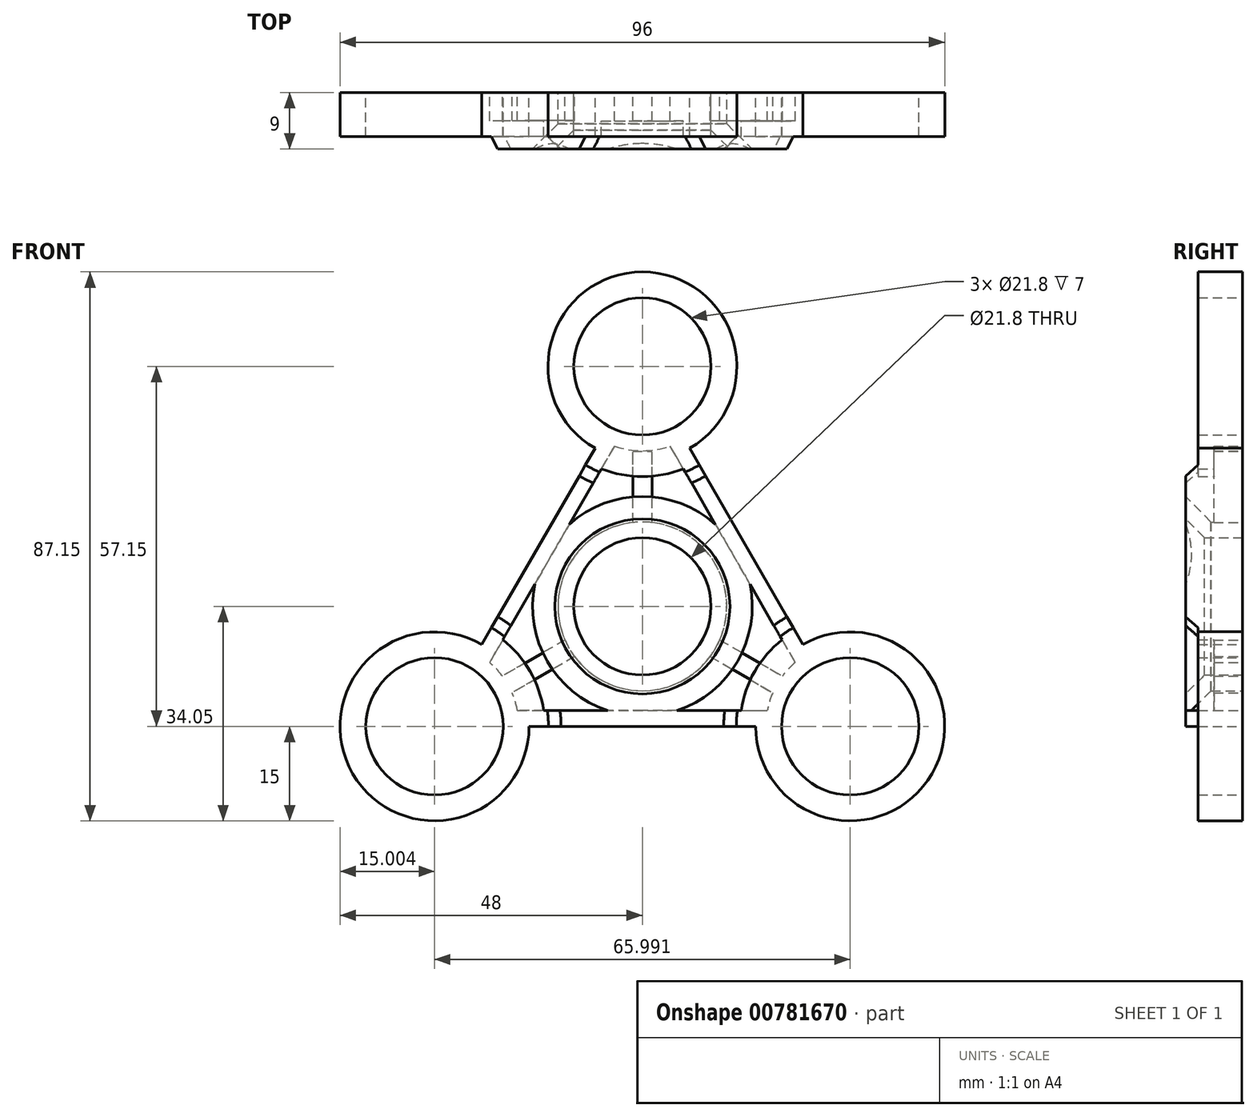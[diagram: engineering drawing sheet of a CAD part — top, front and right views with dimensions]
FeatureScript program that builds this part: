
annotation { "Feature Type Name" : "Feature", "Feature Type Description" : "" }
export const myFeature = defineFeature(function(context is Context, id is Id, definition is map)
    precondition{}
    {
        {
            var Q0;
            Q0=qCreatedBy(makeId("Front.planeOp"),FACE);
            var sketch = newSketch(context, id + "F0", { "sketchPlane" : qUnion([Q0])});
            skPoint(sketch, "E0.middle", {"position": v(0, 0) * mm});
            skLineSegment(sketch, "E1", {"start": v(-33, -19.05) * mm, "end": v(33, -19.05) * mm});
            skLineSegment(sketch, "E2", {"start": v(33, -19.05) * mm, "end": v(0, 38.1) * mm});
            skLineSegment(sketch, "E3", {"start": v(0, 38.1) * mm, "end": v(-33, -19.05) * mm});
            skLineSegment(sketch, "E4", {"start": v(0, 0) * mm, "end": v(-33, -19.05) * mm, "construction": true});
            skLineSegment(sketch, "E5", {"start": v(0, 0) * mm, "end": v(33, -19.05) * mm, "construction": true});
            skLineSegment(sketch, "E6", {"start": v(0, 0) * mm, "end": v(0, 38.1) * mm, "construction": true});
            skCircle(sketch, "E7", {"center": v(0, 0) * mm, "radius": 10.9 * mm});
            skCircle(sketch, "E8", {"center": v(0, 38.1) * mm, "radius": 15 * mm});
            skCircle(sketch, "E9", {"center": v(33, -19.05) * mm, "radius": 15 * mm});
            skCircle(sketch, "E10", {"center": v(-33, -19.05) * mm, "radius": 15 * mm});
            skCircle(sketch, "E11", {"center": v(0, 38.1) * mm, "radius": 10.9 * mm});
            skCircle(sketch, "E12", {"center": v(33, -19.05) * mm, "radius": 10.9 * mm});
            skCircle(sketch, "E13", {"center": v(-33, -19.05) * mm, "radius": 10.9 * mm});
            skSolve(sketch);
        }
        {
            var Q0;
            Q0=makeQuery(id+"F0.imprint","IMPRINT",FACE,{"disambiguationData":[TD([[makeQuery(id+"F0.imprint","IMPRINT",EDGE,{"derivedFrom":sQuery(id+"F0.wireOp",EDGE,"E7")}),-1.0]])]});
            extrude(context, id + "F1", {"entities" : qUnion([Q0]), "depth" : 9 * mm, "offsetDistance" : 25.4 * mm});
        }
        {
            var Q0;
            Q0 = qSketchRegion(id + "F0", true);
            extrude(context, id + "F2", {"entities" : qUnion([Q0]), "operationType" : NewBodyOperationType.ADD, "depth" : 7 * mm, "offsetDistance" : 25.4 * mm});
        }
        {
            var Q0;
            Q0=makeQuery(id+"F1.opExtrude","CAP_EDGE",EDGE,{"disambiguationData":[OSD([sQuery(id+"F0.wireOp",EDGE,"E7")])],"isStart":false});
            chamfer(context, id + "F3", {"entities" : qUnion([Q0]), "width" : 3 * mm, "tangentPropagation" : true});
        }
        {
            var Q0;
            Q0=makeQuery(id+"F1.opExtrude","CAP_FACE",FACE,{"disambiguationData":[OSD([sQuery(id+"F0.wireOp",EDGE,"E1"),sQuery(id+"F0.wireOp",EDGE,"E2"),sQuery(id+"F0.wireOp",EDGE,"E3"),sQuery(id+"F0.wireOp",EDGE,"E7"),sQuery(id+"F0.wireOp",EDGE,"E8"),sQuery(id+"F0.wireOp",EDGE,"E9"),sQuery(id+"F0.wireOp",EDGE,"E10")])],"isStart":false});
            shell(context, id + "F4", {"entities" : qUnion([Q0]), "thickness" : 5 * mm});
        }
        {
            var Q0;
            Q0=makeQuery(id+"F1.opExtrude","CAP_FACE",FACE,{"disambiguationData":[OSD([sQuery(id+"F0.wireOp",EDGE,"E1"),sQuery(id+"F0.wireOp",EDGE,"E2"),sQuery(id+"F0.wireOp",EDGE,"E3"),sQuery(id+"F0.wireOp",EDGE,"E7"),sQuery(id+"F0.wireOp",EDGE,"E8"),sQuery(id+"F0.wireOp",EDGE,"E9"),sQuery(id+"F0.wireOp",EDGE,"E10")])],"isStart":false});
            shell(context, id + "F5", {"entities" : qUnion([Q0]), "thickness" : 2.5 * mm});
        }
        {
            var Q0;
            {var subQ0=sQuery(id+"F0.wireOp",EDGE,"E13");var subQ1=sQuery(id+"F0.wireOp",EDGE,"E12");var subQ2=sQuery(id+"F0.wireOp",EDGE,"E11");var subQ3=sQuery(id+"F0.wireOp",EDGE,"E10");var subQ4=sQuery(id+"F0.wireOp",EDGE,"E9");var subQ5=sQuery(id+"F0.wireOp",EDGE,"E8");var subQ6=sQuery(id+"F0.wireOp",EDGE,"E7");var subQ7=sQuery(id+"F0.wireOp",EDGE,"E3");var subQ8=sQuery(id+"F0.wireOp",EDGE,"E2");var subQ9=sQuery(id+"F0.wireOp",EDGE,"E1");Q0=makeQuery(id+"F5.opShell","OFFSET_FACE",FACE,{"disambiguationData":[OSD([subQ9,subQ8,subQ7,subQ6,subQ5,subQ4,subQ3,subQ2,subQ1,subQ0]),TDD([makeQuery(id+"F2.boolean.opBoolean","MERGE",FACE,{"derivedFrom":[makeQuery(id+"F1.opExtrude","CAP_FACE",FACE,{"disambiguationData":[OSD([subQ9,subQ8,subQ7,subQ6,subQ5,subQ4,subQ3])],"isStart":true}),makeQuery(id+"F2.opExtrude","CAP_FACE",FACE,{"disambiguationData":[OSD([subQ9,subQ8,subQ7,subQ6,subQ5,subQ4,subQ3,subQ2,subQ1,subQ0])],"isStart":true})]})])]});}
            extrude(context, id + "F6", {"entities" : qUnion([Q0]), "operationType" : NewBodyOperationType.REMOVE, "oppositeDirection" : true, "depth" : 25.4 * mm, "offsetDistance" : 25.4 * mm});
        }
        {
            var Q0;
            Q0=makeQuery(id+"F1.opExtrude","CAP_EDGE",EDGE,{"disambiguationData":[OSD([sQuery(id+"F0.wireOp",EDGE,"E8")])],"isStart":false});
            var Q1;
            Q1=makeQuery(id+"F1.opExtrude","CAP_EDGE",EDGE,{"disambiguationData":[OSD([sQuery(id+"F0.wireOp",EDGE,"E9")])],"isStart":false});
            var Q2;
            Q2=makeQuery(id+"F1.opExtrude","CAP_EDGE",EDGE,{"disambiguationData":[OSD([sQuery(id+"F0.wireOp",EDGE,"E10")])],"isStart":false});
            chamfer(context, id + "F7", {"entities" : qUnion([Q0, Q1, Q2]), "width" : 5.08 * mm, "tangentPropagation" : true});
        }
        {
            var Q0;
            Q0=qCreatedBy(makeId("Front.planeOp"),FACE);
            var sketch = newSketch(context, id + "F8", { "sketchPlane" : qUnion([Q0])});
            skLineSegment(sketch, "E14", {"start": v(-1.53, 13.3) * mm, "end": v(-1.53, 24.64) * mm});
            skLineSegment(sketch, "E15.MirrorCS", {"start": v(1.53, 13.3) * mm, "end": v(1.53, 24.64) * mm});
            skLineSegment(sketch, "E16", {"start": v(0, 0) * mm, "end": v(21.16, -12.21) * mm, "construction": true});
            skLineSegment(sketch, "E17.MirrorCS", {"start": v(0, 0) * mm, "end": v(-21.16, -12.21) * mm, "construction": true});
            skLineSegment(sketch, "E18", {"start": v(0, 0) * mm, "end": v(0, 24.62) * mm, "construction": true});
            skLineSegment(sketch, "E19", {"start": v(-12.21, -5.28) * mm, "end": v(-22.32, -11.12) * mm});
            skLineSegment(sketch, "E20", {"start": v(12.18, -5.26) * mm, "end": v(22.32, -11.11) * mm});
            skLineSegment(sketch, "E21.MirrorCS", {"start": v(10.64, -7.91) * mm, "end": v(20.78, -13.77) * mm});
            skLineSegment(sketch, "E22.MirrorCS", {"start": v(-10.68, -7.94) * mm, "end": v(-20.8, -13.77) * mm});
            skLineSegment(sketch, "E23", {"start": v(12.18, -5.26) * mm, "end": v(10.64, -7.91) * mm});
            skLineSegment(sketch, "E24", {"start": v(22.32, -11.11) * mm, "end": v(20.78, -13.77) * mm});
            skLineSegment(sketch, "E25", {"start": v(-20.8, -13.77) * mm, "end": v(-22.32, -11.12) * mm});
            skLineSegment(sketch, "E26", {"start": v(-12.21, -5.28) * mm, "end": v(-10.68, -7.94) * mm});
            skLineSegment(sketch, "E27", {"start": v(-1.53, 13.3) * mm, "end": v(1.53, 13.3) * mm});
            skLineSegment(sketch, "E28", {"start": v(-1.53, 24.64) * mm, "end": v(1.53, 24.64) * mm});
            skSolve(sketch);
        }
        {
            var Q0;
            Q0=makeQuery(id+"F8.imprint","IMPRINT",FACE,{"disambiguationData":[TD([[makeQuery(id+"F8.imprint","IMPRINT",EDGE,{"derivedFrom":sQuery(id+"F8.wireOp",EDGE,"E20")}),-1.0]])]});
            var Q1;
            Q1=makeQuery(id+"F8.imprint","IMPRINT",FACE,{"disambiguationData":[TD([[makeQuery(id+"F8.imprint","IMPRINT",EDGE,{"derivedFrom":sQuery(id+"F8.wireOp",EDGE,"E19")}),1.0]])]});
            var Q2;
            Q2=makeQuery(id+"F8.imprint","IMPRINT",FACE,{"disambiguationData":[TD([[makeQuery(id+"F8.imprint","IMPRINT",EDGE,{"derivedFrom":sQuery(id+"F8.wireOp",EDGE,"E14")}),-1.0]])]});
            extrude(context, id + "F9", {"entities" : qUnion([Q0, Q1, Q2]), "operationType" : NewBodyOperationType.ADD, "depth" : 4.5 * mm, "offsetDistance" : 25.4 * mm});
        }
    });
